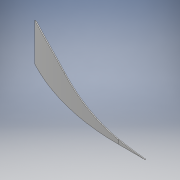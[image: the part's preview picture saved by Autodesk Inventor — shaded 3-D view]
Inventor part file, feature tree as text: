
AUTODESK INVENTOR PART (.ipt)
format: ipt  version: 2018 (Build 220112000, 112)  size: 131,584 bytes
history: native  units: mm
features: other x4, extrude x1, sketch x1, projected_geometry x1
ambient origin geometry x8: Origin, YZ Plane, XZ Plane, XY Plane, X Axis, Y Axis, Z Axis, Center Point
bodies: Body1 (feature_tree)
feature tree (7):
  other  "splitter.ipt"
  extrude  "押し出し1"  Depth=10.0mm
  other  "ソリッド162::splitter.ipt"
  other  "TaggingFeature1"
  sketch  "スケッチ1"
  projected_geometry  "投影ループ1"
  other  "ソリッド1"
